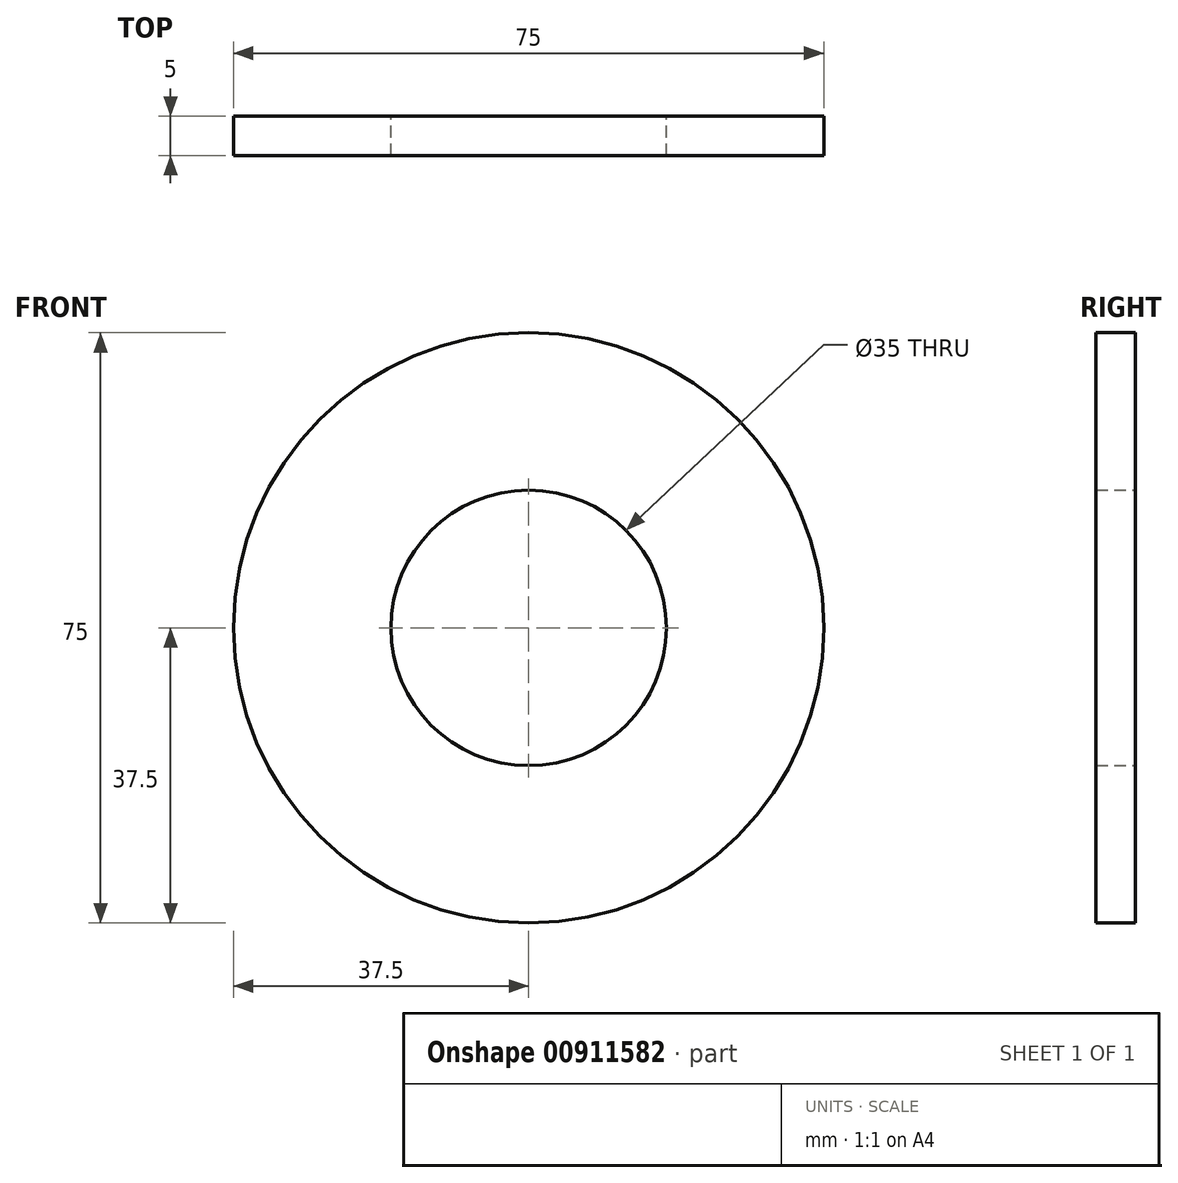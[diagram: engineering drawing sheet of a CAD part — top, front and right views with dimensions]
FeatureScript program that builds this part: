
annotation { "Feature Type Name" : "Feature", "Feature Type Description" : "" }
export const myFeature = defineFeature(function(context is Context, id is Id, definition is map)
    precondition{}
    {
        {
            var Q0;
            Q0=qCreatedBy(makeId("Front.planeOp"),FACE);
            var sketch = newSketch(context, id + "F0", { "sketchPlane" : qUnion([Q0])});
            skCircle(sketch, "E0", {"center": v(0, 0) * mm, "radius": 37.5 * mm});
            skCircle(sketch, "E1", {"center": v(0, 0) * mm, "radius": 17.5 * mm});
            skSolve(sketch);
        }
        {
            var Q0;
            Q0=makeQuery(id+"F0.imprint","IMPRINT",FACE,{"disambiguationData":[TD([[makeQuery(id+"F0.imprint","IMPRINT",EDGE,{"derivedFrom":sQuery(id+"F0.wireOp",EDGE,"E0")}),1.0]])]});
            extrude(context, id + "F1", {"entities" : qUnion([Q0]), "depth" : 5 * mm, "offsetDistance" : 25 * mm});
        }
    });
